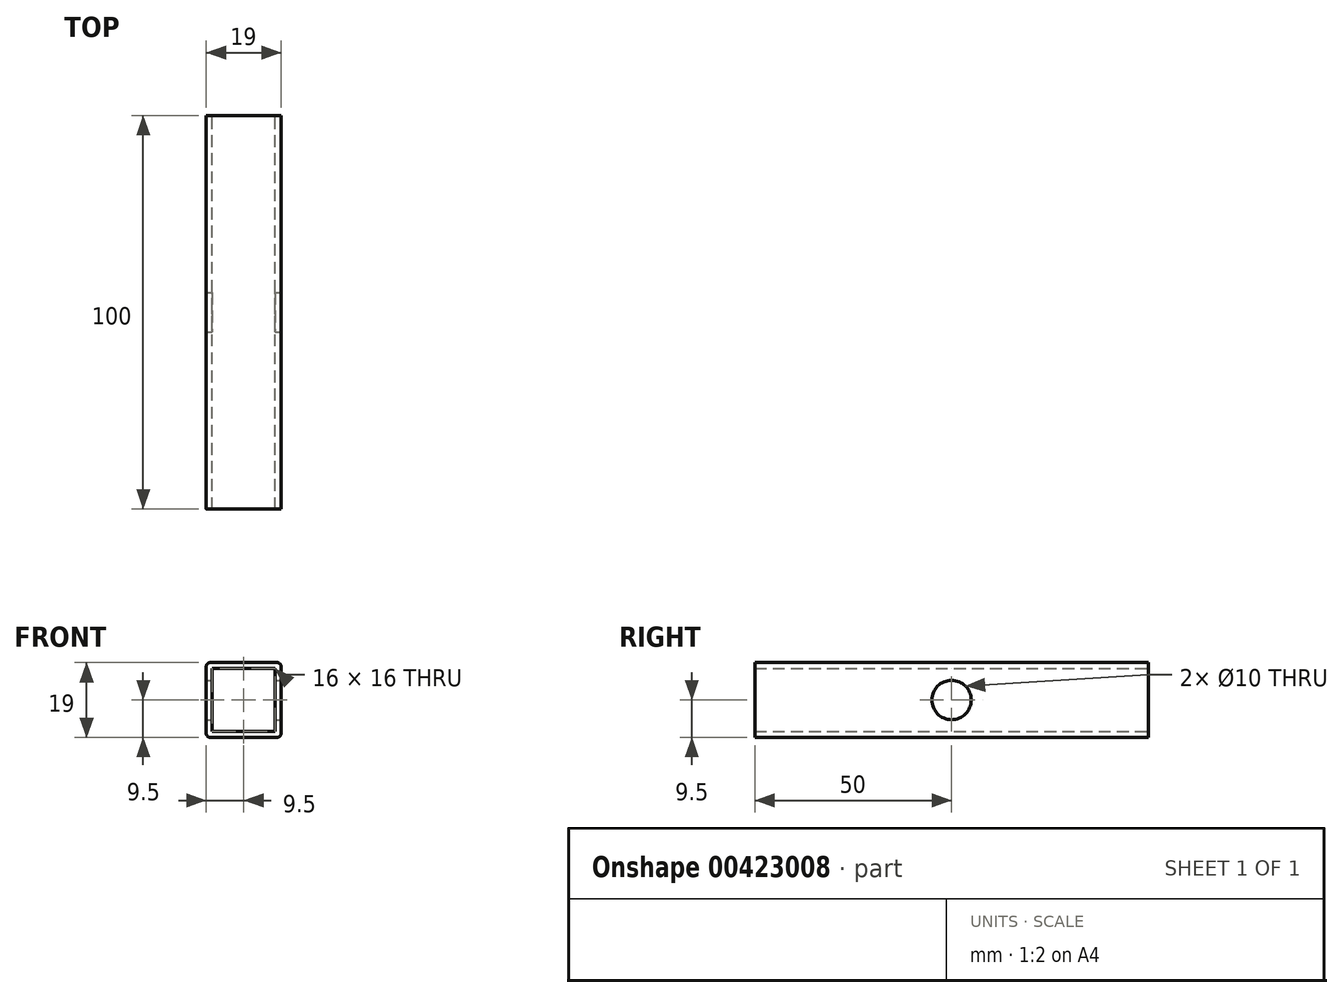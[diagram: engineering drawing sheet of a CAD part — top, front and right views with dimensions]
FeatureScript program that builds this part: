
annotation { "Feature Type Name" : "Feature", "Feature Type Description" : "" }
export const myFeature = defineFeature(function(context is Context, id is Id, definition is map)
    precondition{}
    {
        {
            var Q0;
            Q0=qCreatedBy(makeId("Front.planeOp"),FACE);
            var sketch = newSketch(context, id + "F0", { "sketchPlane" : qUnion([Q0])});
            skLineSegment(sketch, "E0.bottom", {"start": v(-8, 8) * mm, "end": v(8, 8) * mm});
            skLineSegment(sketch, "E0.top", {"start": v(-8, -8) * mm, "end": v(8, -8) * mm});
            skLineSegment(sketch, "E0.left", {"start": v(-8, 8) * mm, "end": v(-8, -8) * mm});
            skLineSegment(sketch, "E0.right", {"start": v(8, 8) * mm, "end": v(8, -8) * mm});
            skLineSegment(sketch, "E1.bottom", {"start": v(-9.5, 9.5) * mm, "end": v(9.5, 9.5) * mm});
            skLineSegment(sketch, "E1.top", {"start": v(-9.5, -9.5) * mm, "end": v(9.5, -9.5) * mm});
            skLineSegment(sketch, "E1.left", {"start": v(-9.5, 9.5) * mm, "end": v(-9.5, -9.5) * mm});
            skLineSegment(sketch, "E1.right", {"start": v(9.5, 9.5) * mm, "end": v(9.5, -9.5) * mm});
            skLineSegment(sketch, "E2", {"start": v(-9.5, 9.5) * mm, "end": v(9.5, -9.5) * mm, "construction": true});
            skLineSegment(sketch, "E3", {"start": v(9.5, 9.5) * mm, "end": v(-9.5, -9.5) * mm, "construction": true});
            skSolve(sketch);
        }
        {
            var Q0;
            Q0=qCreatedBy(makeId("Right.planeOp"),FACE);
            var sketch = newSketch(context, id + "F1", { "sketchPlane" : qUnion([Q0])});
            skCircle(sketch, "E4", {"center": v(0, 0) * mm, "radius": 5 * mm});
            skSolve(sketch);
        }
        {
            var Q0;
            Q0=makeQuery(id+"F0.imprint","IMPRINT",FACE,{"disambiguationData":[TD([[makeQuery(id+"F0.imprint","IMPRINT",EDGE,{"derivedFrom":sQuery(id+"F0.wireOp",EDGE,"E0.bottom")}),1.0]])]});
            extrude(context, id + "F2", {"entities" : qUnion([Q0]), "endBound" : BoundingType.SYMMETRIC, "depth" : 100 * mm});
        }
        {
            var Q0;
            Q0 = qSketchRegion(id + "F1", true);
            var Q1;
            Q1=sQuery(id+"F1.wireOp",EDGE,"E4");
            extrude(context, id + "F3", {"entities" : qUnion([Q0]), "operationType" : NewBodyOperationType.REMOVE, "surfaceEntities" : qUnion([Q1]), "endBound" : BoundingType.SYMMETRIC, "oppositeDirection" : true, "depth" : 25 * mm});
        }
        {
            var Q0;
            Q0=makeQuery(id+"F2.opExtrude","SWEPT_EDGE",EDGE,{"disambiguationData":[OSD([sQuery(id+"F0.wireOp",EDGE,"E1.bottom"),sQuery(id+"F0.wireOp",EDGE,"E1.right")])]});
            var Q1;
            Q1=makeQuery(id+"F2.opExtrude","SWEPT_EDGE",EDGE,{"disambiguationData":[OSD([sQuery(id+"F0.wireOp",EDGE,"E1.bottom"),sQuery(id+"F0.wireOp",EDGE,"E1.left")])]});
            var Q2;
            Q2=makeQuery(id+"F2.opExtrude","SWEPT_EDGE",EDGE,{"disambiguationData":[OSD([sQuery(id+"F0.wireOp",EDGE,"E1.top"),sQuery(id+"F0.wireOp",EDGE,"E1.right")])]});
            var Q3;
            Q3=makeQuery(id+"F2.opExtrude","SWEPT_EDGE",EDGE,{"disambiguationData":[OSD([sQuery(id+"F0.wireOp",EDGE,"E1.top"),sQuery(id+"F0.wireOp",EDGE,"E1.left")])]});
            fillet(context, id + "F4", {"entities" : qUnion([Q0, Q1, Q2, Q3]), "radius" : 1 * mm, "tangentPropagation" : true, "allowEdgeOverflow" : false});
        }
    });
